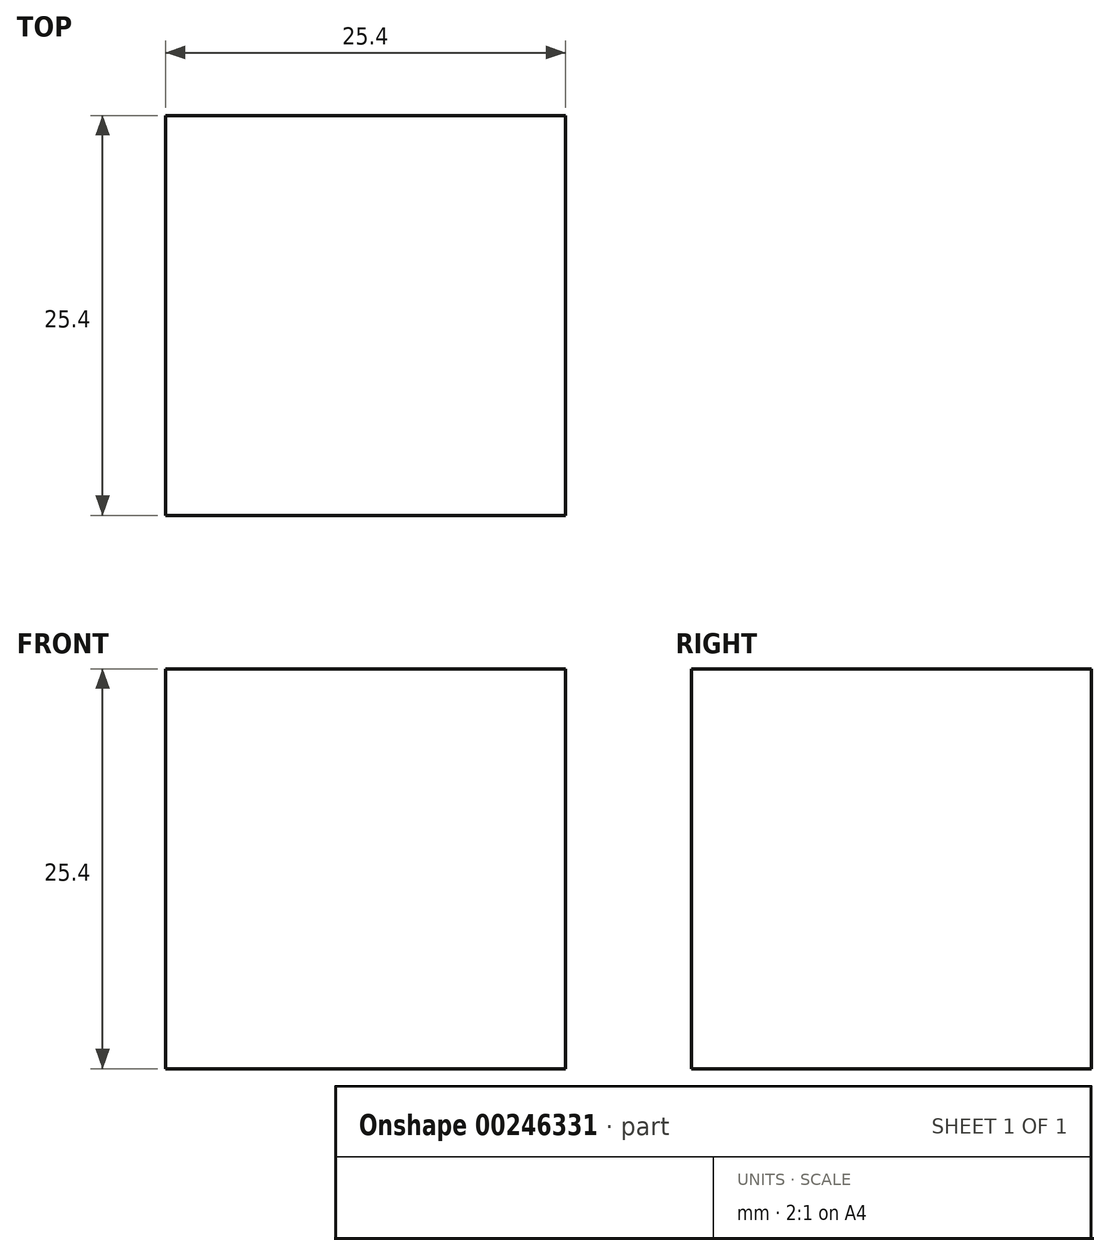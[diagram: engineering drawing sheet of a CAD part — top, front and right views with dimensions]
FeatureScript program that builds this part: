
annotation { "Feature Type Name" : "Feature", "Feature Type Description" : "" }
export const myFeature = defineFeature(function(context is Context, id is Id, definition is map)
    precondition{}
    {
        {
            var Q0;
            Q0=qCreatedBy(makeId("Front.planeOp"),FACE);
            var sketch = newSketch(context, id + "F0", { "sketchPlane" : qUnion([Q0])});
            skLineSegment(sketch, "E0.bottom", {"start": v(-16.41, 12.7) * mm, "end": v(8.99, 12.7) * mm});
            skLineSegment(sketch, "E0.top", {"start": v(-16.41, -12.7) * mm, "end": v(8.99, -12.7) * mm});
            skLineSegment(sketch, "E0.left", {"start": v(-16.41, 12.7) * mm, "end": v(-16.41, -12.7) * mm});
            skLineSegment(sketch, "E0.right", {"start": v(8.99, 12.7) * mm, "end": v(8.99, -12.7) * mm});
            skSolve(sketch);
        }
        {
            var Q0;
            Q0=makeQuery(id+"F0.imprint","IMPRINT",FACE,{"disambiguationData":[TD([[makeQuery(id+"F0.imprint","IMPRINT",EDGE,{"derivedFrom":sQuery(id+"F0.wireOp",EDGE,"E0.bottom")}),-1.0]])]});
            extrude(context, id + "F1", {"entities" : qUnion([Q0]), "depth" : 25.4 * mm});
        }
    });
